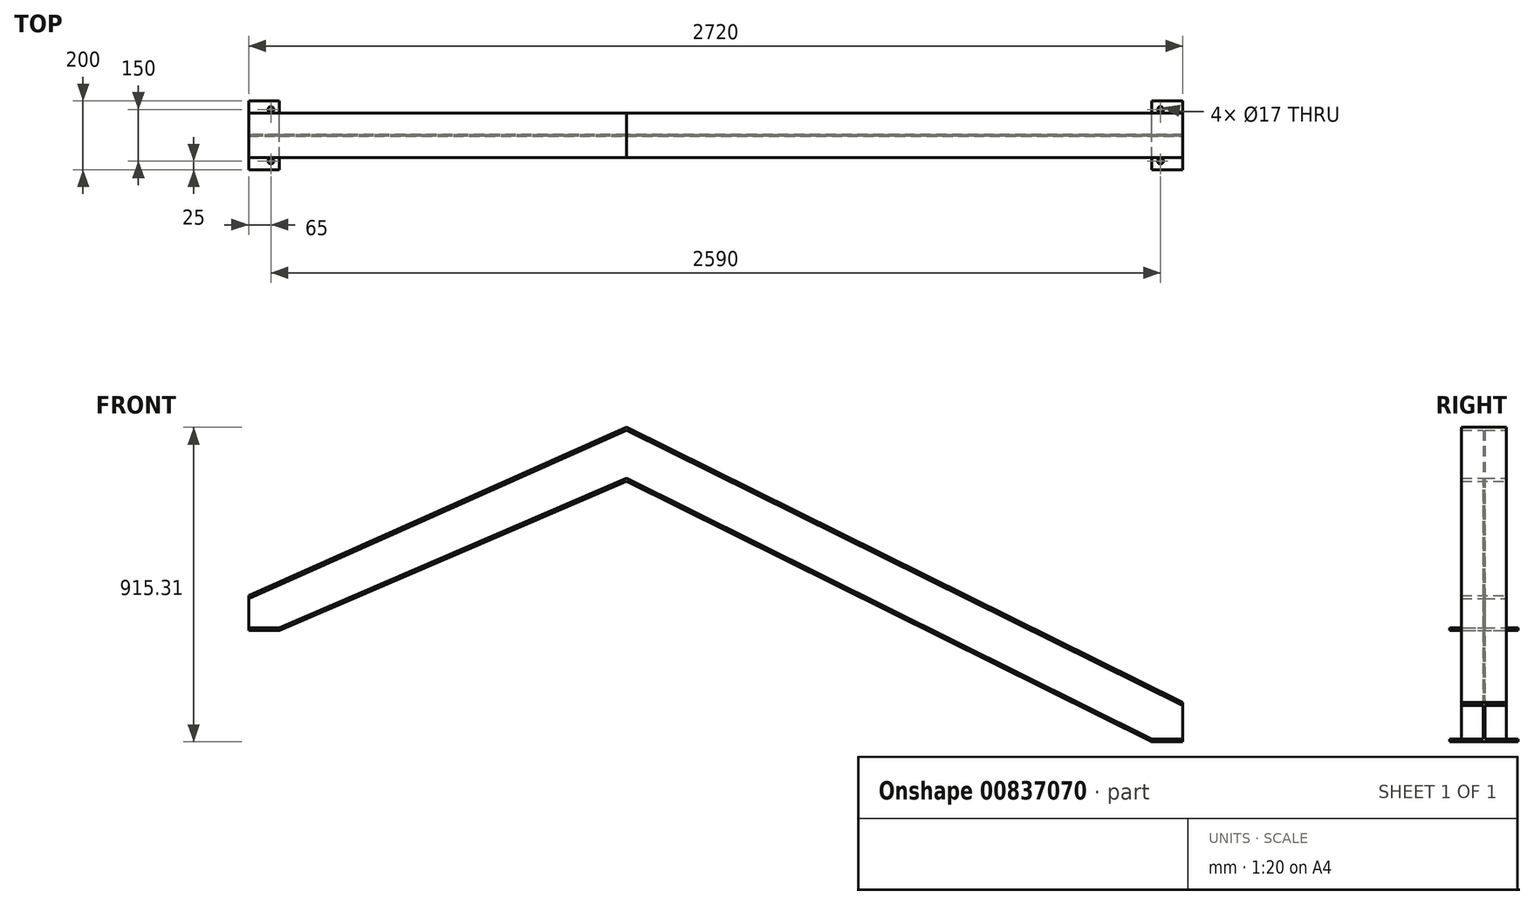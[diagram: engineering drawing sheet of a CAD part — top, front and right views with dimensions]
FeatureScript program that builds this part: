
annotation { "Feature Type Name" : "Feature", "Feature Type Description" : "" }
export const myFeature = defineFeature(function(context is Context, id is Id, definition is map)
    precondition{}
    {
        {
            var Q0;
            Q0=qCreatedBy(makeId("Front.planeOp"),FACE);
            var sketch = newSketch(context, id + "F0", { "sketchPlane" : qUnion([Q0])});
            skLineSegment(sketch, "E0", {"start": v(0, 489.75) * mm, "end": v(-1100, 0) * mm});
            skLineSegment(sketch, "E1", {"start": v(-1100, 0) * mm, "end": v(-1100, -85) * mm});
            skLineSegment(sketch, "E2", {"start": v(0, 489.75) * mm, "end": v(1620, -310.9) * mm});
            skLineSegment(sketch, "E3", {"start": v(1620, -310.9) * mm, "end": v(1620, -408.8) * mm});
            skLineSegment(sketch, "E4", {"start": v(-1100, -85) * mm, "end": v(-1010, -85) * mm});
            skLineSegment(sketch, "E5", {"start": v(-1010, -85) * mm, "end": v(0, 349.75) * mm});
            skLineSegment(sketch, "E6", {"start": v(1620, -408.8) * mm, "end": v(1530, -408.8) * mm});
            skLineSegment(sketch, "E7", {"start": v(1530, -408.8) * mm, "end": v(0, 349.75) * mm});
            skSolve(sketch);
        }
        {
            var Q0;
            Q0 = qSketchRegion(id + "F0", true);
            extrude(context, id + "F1", {"entities" : qUnion([Q0]), "depth" : 5 * mm, "offsetDistance" : 25 * mm, "symmetric" : true});
        }
        {
            var Q0;
            Q0=qCreatedBy(makeId("Front.planeOp"),FACE);
            var sketch = newSketch(context, id + "F2", { "sketchPlane" : qUnion([Q0])});
            skLineSegment(sketch, "E8", {"start": v(-1100, 0) * mm, "end": v(0, 489.75) * mm});
            skLineSegment(sketch, "E9", {"start": v(0, 489.75) * mm, "end": v(1620, -310.9) * mm});
            skLineSegment(sketch, "E10", {"start": v(1620, -310.9) * mm, "end": v(1620, -302.15) * mm});
            skLineSegment(sketch, "E11", {"start": v(1620, -302.15) * mm, "end": v(0, 498.5) * mm});
            skLineSegment(sketch, "E12", {"start": v(0, 498.5) * mm, "end": v(-1100, 8.76) * mm});
            skLineSegment(sketch, "E13", {"start": v(-1100, 8.76) * mm, "end": v(-1100, 0) * mm});
            skLineSegment(sketch, "E14", {"start": v(-1100, 0) * mm, "end": v(-1100, -8.14) * mm});
            skLineSegment(sketch, "E15", {"start": v(1620, -310.9) * mm, "end": v(1620, -170.6) * mm});
            skLineSegment(sketch, "E16", {"start": v(0, 349.75) * mm, "end": v(-1010, -85) * mm});
            skLineSegment(sketch, "E17", {"start": v(-1010, -85) * mm, "end": v(-1100, -85) * mm});
            skLineSegment(sketch, "E18", {"start": v(-1100, -85) * mm, "end": v(-1100, -93) * mm});
            skLineSegment(sketch, "E19", {"start": v(-1100, -93) * mm, "end": v(-1010, -93) * mm});
            skLineSegment(sketch, "E20", {"start": v(-1010, -93) * mm, "end": v(0, 341.75) * mm});
            skLineSegment(sketch, "E21", {"start": v(0, 349.75) * mm, "end": v(1530, -408.8) * mm});
            skLineSegment(sketch, "E22", {"start": v(1530, -408.8) * mm, "end": v(1620, -408.8) * mm});
            skLineSegment(sketch, "E23", {"start": v(1620, -408.8) * mm, "end": v(1620, -416.8) * mm});
            skLineSegment(sketch, "E24", {"start": v(1620, -416.8) * mm, "end": v(1530, -416.8) * mm});
            skLineSegment(sketch, "E25", {"start": v(1530, -416.8) * mm, "end": v(0, 341.75) * mm});
            skSolve(sketch);
        }
        {
            var Q0;
            Q0 = qSketchRegion(id + "F2", true);
            extrude(context, id + "F3", {"entities" : qUnion([Q0]), "operationType" : NewBodyOperationType.ADD, "depth" : 130 * mm, "offsetDistance" : 25 * mm, "symmetric" : true});
        }
        {
            var Q0;
            Q0=makeQuery(id+"F3.opExtrude","SWEPT_FACE",FACE,{"disambiguationData":[OSD([sQuery(id+"F2.wireOp",EDGE,"E19")])]});
            var sketch = newSketch(context, id + "F4", { "sketchPlane" : qUnion([Q0])});
            skLineSegment(sketch, "E26.bottom", {"start": v(-1100, -100) * mm, "end": v(-1010, -100) * mm});
            skLineSegment(sketch, "E26.top", {"start": v(-1100, 100) * mm, "end": v(-1010, 100) * mm});
            skLineSegment(sketch, "E26.left", {"start": v(-1100, -100) * mm, "end": v(-1100, 100) * mm});
            skLineSegment(sketch, "E26.right", {"start": v(-1010, -100) * mm, "end": v(-1010, 100) * mm});
            skLineSegment(sketch, "E27", {"start": v(-1100, 0) * mm, "end": v(-1010, 0) * mm, "construction": true});
            skCircle(sketch, "E28", {"center": v(-1035, -75) * mm, "radius": 8.5 * mm});
            skCircle(sketch, "E29.MirrorC", {"center": v(-1035, 75) * mm, "radius": 8.5 * mm});
            skSolve(sketch);
        }
        {
            var Q0;
            Q0 = qSketchRegion(id + "F4", true);
            extrude(context, id + "F5", {"entities" : qUnion([Q0]), "operationType" : NewBodyOperationType.ADD, "oppositeDirection" : true, "depth" : 8 * mm, "offsetDistance" : 25 * mm});
        }
        {
            var Q0;
            Q0=makeQuery(id+"F3.opExtrude","SWEPT_FACE",FACE,{"disambiguationData":[OSD([sQuery(id+"F2.wireOp",EDGE,"E24")])]});
            var sketch = newSketch(context, id + "F6", { "sketchPlane" : qUnion([Q0])});
            skLineSegment(sketch, "E30.bottom", {"start": v(1620, -100) * mm, "end": v(1530, -100) * mm});
            skLineSegment(sketch, "E30.top", {"start": v(1620, 100) * mm, "end": v(1530, 100) * mm});
            skLineSegment(sketch, "E30.left", {"start": v(1620, -100) * mm, "end": v(1620, 100) * mm});
            skLineSegment(sketch, "E30.right", {"start": v(1530, -100) * mm, "end": v(1530, 100) * mm});
            skLineSegment(sketch, "E31", {"start": v(1620, 0) * mm, "end": v(1530, 0) * mm, "construction": true});
            skCircle(sketch, "E32", {"center": v(1555, 75) * mm, "radius": 8.5 * mm});
            skCircle(sketch, "E33.MirrorC", {"center": v(1555, -75) * mm, "radius": 8.5 * mm});
            skSolve(sketch);
        }
        {
            var Q0;
            Q0 = qSketchRegion(id + "F6", true);
            extrude(context, id + "F7", {"entities" : qUnion([Q0]), "operationType" : NewBodyOperationType.ADD, "oppositeDirection" : true, "depth" : 8 * mm, "offsetDistance" : 25 * mm});
        }
    });
